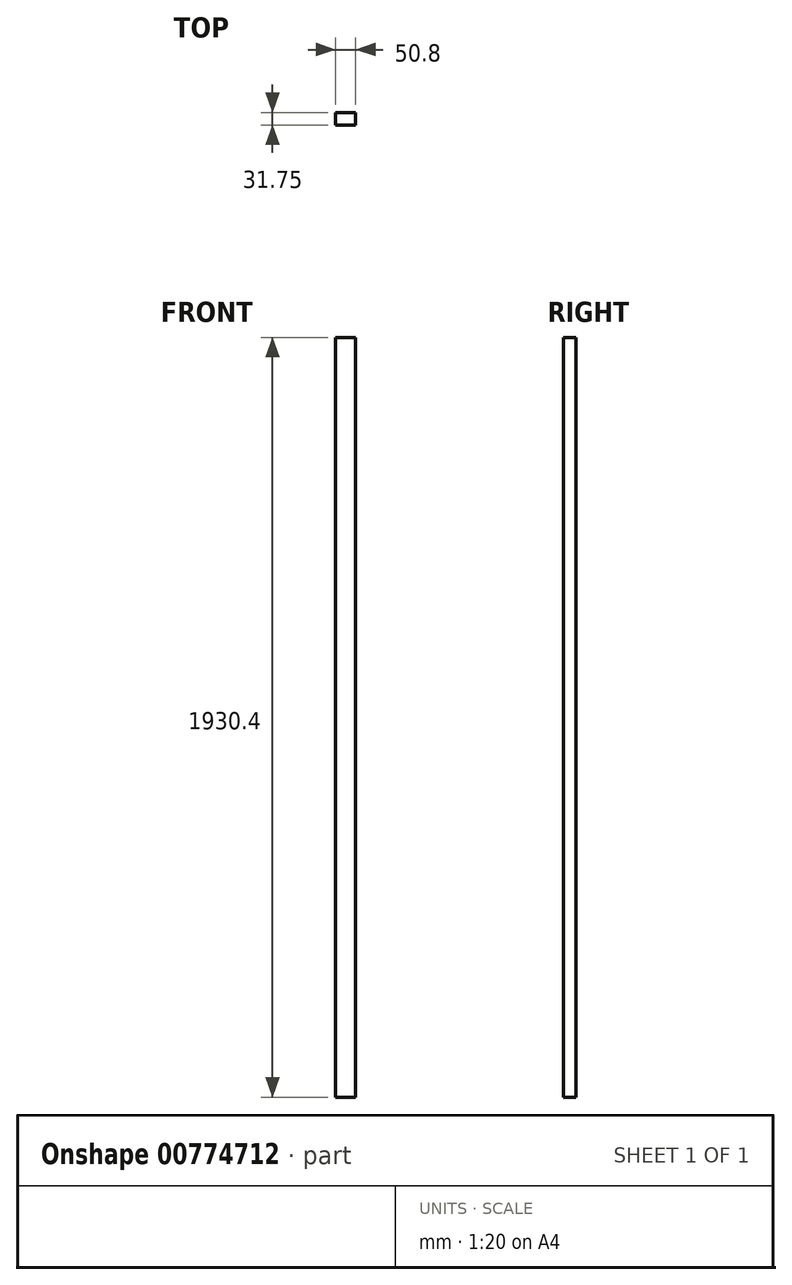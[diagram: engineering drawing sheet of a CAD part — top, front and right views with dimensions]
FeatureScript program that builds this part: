
annotation { "Feature Type Name" : "Feature", "Feature Type Description" : "" }
export const myFeature = defineFeature(function(context is Context, id is Id, definition is map)
    precondition{}
    {
        {
            var Q0;
            Q0=qCreatedBy(makeId("Top.planeOp"),FACE);
            var sketch = newSketch(context, id + "F0", { "sketchPlane" : qUnion([Q0])});
            skLineSegment(sketch, "E0.bottom", {"start": v(0, 0) * mm, "end": v(50.8, 0) * mm});
            skLineSegment(sketch, "E0.top", {"start": v(0, 31.75) * mm, "end": v(50.8, 31.75) * mm});
            skLineSegment(sketch, "E0.left", {"start": v(0, 0) * mm, "end": v(0, 31.75) * mm});
            skLineSegment(sketch, "E0.right", {"start": v(50.8, 0) * mm, "end": v(50.8, 31.75) * mm});
            skSolve(sketch);
        }
        {
            var Q0;
            Q0 = qSketchRegion(id + "F0", true);
            extrude(context, id + "F1", {"entities" : qUnion([Q0]), "depth" : 1930.4 * mm, "offsetDistance" : 25.4 * mm});
        }
    });
